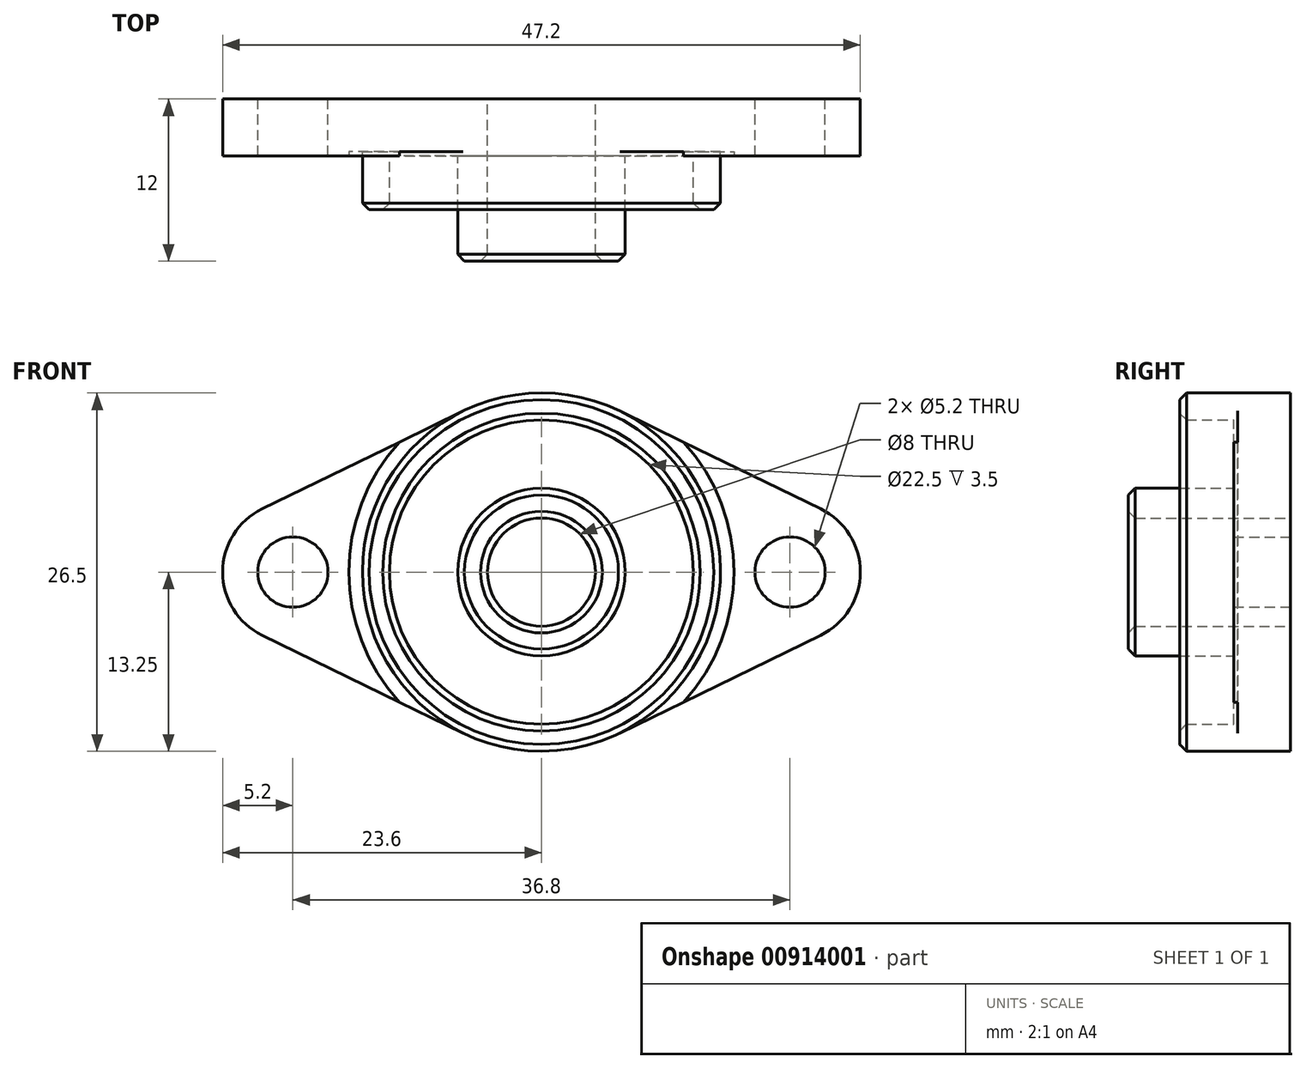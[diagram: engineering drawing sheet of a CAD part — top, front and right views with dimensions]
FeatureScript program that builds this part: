
annotation { "Feature Type Name" : "Feature", "Feature Type Description" : "" }
export const myFeature = defineFeature(function(context is Context, id is Id, definition is map)
    precondition{}
    {
        {
            var Q0;
            Q0=qCreatedBy(makeId("Front.planeOp"),FACE);
            var sketch = newSketch(context, id + "F0", { "sketchPlane" : qUnion([Q0])});
            skCircle(sketch, "E0", {"center": v(0, 0) * mm, "radius": 4 * mm});
            skCircle(sketch, "E1", {"center": v(0, 0) * mm, "radius": 13.25 * mm});
            skLineSegment(sketch, "E2", {"start": v(-18.4, 0) * mm, "end": v(0, 0) * mm, "construction": true});
            skLineSegment(sketch, "E3", {"start": v(0, 0) * mm, "end": v(18.4, 0) * mm, "construction": true});
            skCircle(sketch, "E4", {"center": v(-18.4, 0) * mm, "radius": 2.6 * mm});
            skCircle(sketch, "E5", {"center": v(18.4, 0) * mm, "radius": 2.6 * mm});
            skLineSegment(sketch, "E6", {"start": v(-5.8, 11.91) * mm, "end": v(-20.68, 4.68) * mm});
            skLineSegment(sketch, "E7", {"start": v(-5.8, -11.91) * mm, "end": v(-20.68, -4.68) * mm});
            skArc(sketch, "E8", {"start": v(-20.68, 4.68) * mm, "mid": v(-23.6, 0) * mm, "end": v(-20.68, -4.68) * mm});
            skArc(sketch, "E9", {"start": v(20.68, 4.68) * mm, "mid": v(23.6, 0) * mm, "end": v(20.68, -4.68) * mm});
            skLineSegment(sketch, "E10", {"start": v(20.68, 4.68) * mm, "end": v(5.8, 11.91) * mm});
            skLineSegment(sketch, "E11", {"start": v(5.8, -11.91) * mm, "end": v(20.68, -4.68) * mm});
            skPoint(sketch, "E12", {"position": v(-13.25, 0) * mm});
            skPoint(sketch, "E13", {"position": v(13.25, 0) * mm});
            skPoint(sketch, "E14", {"position": v(-15.8, 0) * mm});
            skPoint(sketch, "E15", {"position": v(15.8, 0) * mm});
            skSolve(sketch);
        }
        {
            var Q0;
            Q0=makeQuery(id+"F0.imprint","IMPRINT",FACE,{"disambiguationData":[TD([[makeQuery(id+"F0.imprint","IMPRINT",EDGE,{"derivedFrom":sQuery(id+"F0.wireOp",EDGE,"E4")}),-1.0]])]});
            var Q1;
            Q1=makeQuery(id+"F0.imprint","IMPRINT",FACE,{"disambiguationData":[TD([[makeQuery(id+"F0.imprint","IMPRINT",EDGE,{"derivedFrom":sQuery(id+"F0.wireOp",EDGE,"E0")}),-1.0]])]});
            var Q2;
            Q2=makeQuery(id+"F0.imprint","IMPRINT",FACE,{"disambiguationData":[TD([[makeQuery(id+"F0.imprint","IMPRINT",EDGE,{"derivedFrom":sQuery(id+"F0.wireOp",EDGE,"E5")}),-1.0]])]});
            extrude(context, id + "F1", {"entities" : qUnion([Q0, Q1, Q2]), "depth" : 4.2 * mm, "offsetDistance" : 25 * mm});
        }
        {
            var Q0;
            Q0=makeQuery(id+"F1.opExtrude","CAP_FACE",FACE,{"disambiguationData":[OSD([sQuery(id+"F0.wireOp",EDGE,"E0"),sQuery(id+"F0.wireOp",EDGE,"E1"),sQuery(id+"F0.wireOp",EDGE,"E4"),sQuery(id+"F0.wireOp",EDGE,"E5"),sQuery(id+"F0.wireOp",EDGE,"E6"),sQuery(id+"F0.wireOp",EDGE,"E7"),sQuery(id+"F0.wireOp",EDGE,"E8"),sQuery(id+"F0.wireOp",EDGE,"E9"),sQuery(id+"F0.wireOp",EDGE,"E10"),sQuery(id+"F0.wireOp",EDGE,"E11")])],"isStart":false});
            var sketch = newSketch(context, id + "F2", { "sketchPlane" : qUnion([Q0])});
            skCircle(sketch, "E16.0", {"center": v(0, 0) * mm, "radius": 13.25 * mm});
            skCircle(sketch, "E17", {"center": v(0, 0) * mm, "radius": 14.25 * mm});
            skSolve(sketch);
        }
        {
            var Q0;
            Q0 = qSketchRegion(id + "F2", true);
            extrude(context, id + "F3", {"entities" : qUnion([Q0]), "operationType" : NewBodyOperationType.REMOVE, "oppositeDirection" : true, "depth" : 0.3 * mm, "offsetDistance" : 25 * mm});
        }
        {
            var Q0;
            {var subQ0=sQuery(id+"F0.wireOp",EDGE,"E0");var subQ1=sQuery(id+"F0.wireOp",EDGE,"E6");var subQ2=sQuery(id+"F0.wireOp",EDGE,"E1");var subQ3=sQuery(id+"F0.wireOp",EDGE,"E10");var subQ4=sQuery(id+"F0.wireOp",EDGE,"E7");var subQ5=sQuery(id+"F0.wireOp",EDGE,"E11");Q0=makeQuery(id+"F3.boolean.opBoolean","SPLIT",FACE,{"disambiguationData":[TD([makeQuery(id+"F1.opExtrude","SWEPT_FACE",FACE,{"disambiguationData":[OSD([subQ0])]})])],"derivedFrom":makeQuery(id+"F1.opExtrude","CAP_FACE",FACE,{"disambiguationData":[OSD([subQ0,subQ2,sQuery(id+"F0.wireOp",EDGE,"E4"),sQuery(id+"F0.wireOp",EDGE,"E5"),subQ1,subQ4,sQuery(id+"F0.wireOp",EDGE,"E8"),sQuery(id+"F0.wireOp",EDGE,"E9"),subQ3,subQ5])],"isStart":false})});}
            var sketch = newSketch(context, id + "F4", { "sketchPlane" : qUnion([Q0])});
            skCircle(sketch, "E18.0", {"center": v(0, 0) * mm, "radius": 4 * mm});
            skCircle(sketch, "E19", {"center": v(0, 0) * mm, "radius": 6.2 * mm});
            skCircle(sketch, "E20.0", {"center": v(0, 0) * mm, "radius": 13.25 * mm});
            skCircle(sketch, "E21", {"center": v(0, 0) * mm, "radius": 11.25 * mm});
            skSolve(sketch);
        }
        {
            var Q0;
            Q0=makeQuery(id+"F4.imprint","IMPRINT",FACE,{"disambiguationData":[TD([[makeQuery(id+"F4.imprint","IMPRINT",EDGE,{"derivedFrom":sQuery(id+"F4.wireOp",EDGE,"E18.0")}),-1.0]])]});
            extrude(context, id + "F5", {"entities" : qUnion([Q0]), "operationType" : NewBodyOperationType.ADD, "depth" : (12 - 4.2) * mm, "offsetDistance" : 25 * mm});
        }
        {
            var Q0;
            Q0=makeQuery(id+"F4.imprint","IMPRINT",FACE,{"disambiguationData":[TD([[makeQuery(id+"F4.imprint","IMPRINT",EDGE,{"derivedFrom":sQuery(id+"F4.wireOp",EDGE,"E20.0")}),1.0]])]});
            extrude(context, id + "F6", {"entities" : qUnion([Q0]), "operationType" : NewBodyOperationType.ADD, "depth" : 4 * mm, "offsetDistance" : 25 * mm});
        }
        {
            var Q0;
            Q0=makeQuery(id+"F5.opExtrude","CAP_EDGE",EDGE,{"disambiguationData":[OSD([sQuery(id+"F4.wireOp",EDGE,"E18.0")])],"isStart":false});
            var Q1;
            Q1=makeQuery(id+"F5.opExtrude","CAP_EDGE",EDGE,{"disambiguationData":[OSD([sQuery(id+"F4.wireOp",EDGE,"E19")])],"isStart":false});
            var Q2;
            Q2=makeQuery(id+"F6.opExtrude","CAP_EDGE",EDGE,{"disambiguationData":[OSD([sQuery(id+"F4.wireOp",EDGE,"E21")])],"isStart":false});
            var Q3;
            Q3=makeQuery(id+"F6.opExtrude","CAP_EDGE",EDGE,{"disambiguationData":[OSD([sQuery(id+"F4.wireOp",EDGE,"E20.0")])],"isStart":false});
            chamfer(context, id + "F7", {"entities" : qUnion([Q0, Q1, Q2, Q3]), "width" : 0.5 * mm, "tangentPropagation" : true});
        }
    });
